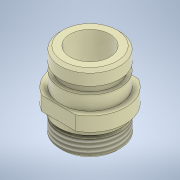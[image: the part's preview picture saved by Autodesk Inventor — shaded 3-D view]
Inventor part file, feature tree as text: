
AUTODESK INVENTOR PART (.ipt)
format: ipt  version: 2020.3 (Build 243373000, 373)  size: 194,560 bytes
history: native  units: mm
features: sketch x3, chamfer x2, extrude x2, revolve x1, thread x1
ambient origin geometry x8: Origin, YZ Plane, XZ Plane, XY Plane, X Axis, Y Axis, Z Axis, Center Point
bodies: Solid1 (feature_tree)
feature tree (9):
  revolve  "Revolution1"  [1 undecoded]
  thread  "Thread1"  [1 undecoded]
  chamfer  "Chamfer1"  Distance=2.0mm
  extrude  "Extrusion1"  Depth=11.0mm
  chamfer  "Chamfer2"  Distance=1.5mm
  extrude  "Extrusion2"  TaperAngle=90.0deg  [1 undecoded]
  sketch  "Sketch1"  dims[d0=10.6mm d1=6.0mm d2=9.0mm]
  sketch  "Sketch2"  dims[d3=1.5mm]
  sketch  "Sketch3"  dims[d4=2.0mm d5=2.0mm d7=11.0mm d8=1.5mm d9=90.0deg d10=5.0mm d11=10.5mm d12=2.0mm d13=5.0mm d14=9.2mm d15=1.3mm d16=2.6mm d17=1.3mm d18=5.0mm d19=90.0deg d20=6.0mm d21=0.0mm d22=1.0mm d23=2.0mm d24=45.0deg d25=14.0mm d26=0.0mm d27=0.0mm d28=1.0mm d29=2.0mm d30=45.0deg d31=22.0mm d32=12.6mm d33=0.0mm d34=0.5mm d35=0.872665mm]
note: 3 required parameter values undecoded (feature->parameter linkage not recoverable at this tier; creation-order binding heuristic only, values carry confidence <= 0.55)